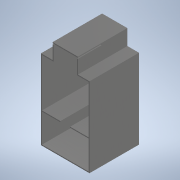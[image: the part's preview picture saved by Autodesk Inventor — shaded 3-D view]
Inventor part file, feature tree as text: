
AUTODESK INVENTOR PART (.ipt)
format: ipt  version: 2020 (Build 240168000, 168)  size: 194,048 bytes
history: native  units: mm
features: extrude x3, sketch x3, projected_geometry x2, other x1
ambient origin geometry x8: Origin, YZ Plane, XZ Plane, XY Plane, X Axis, Y Axis, Z Axis, Center Point
bodies: Body1 (feature_tree)
feature tree (9):
  other  "솔리드1"
  extrude  "돌출1"  Depth=500.0mm
  extrude  "돌출2"  Depth=820.0mm
  extrude  "돌출3"  Depth=820.0mm
  sketch  "스케치1"
  sketch  "스케치2"
  projected_geometry  "투영된 루프1"
  sketch  "스케치3"
  projected_geometry  "투영된 루프2"
